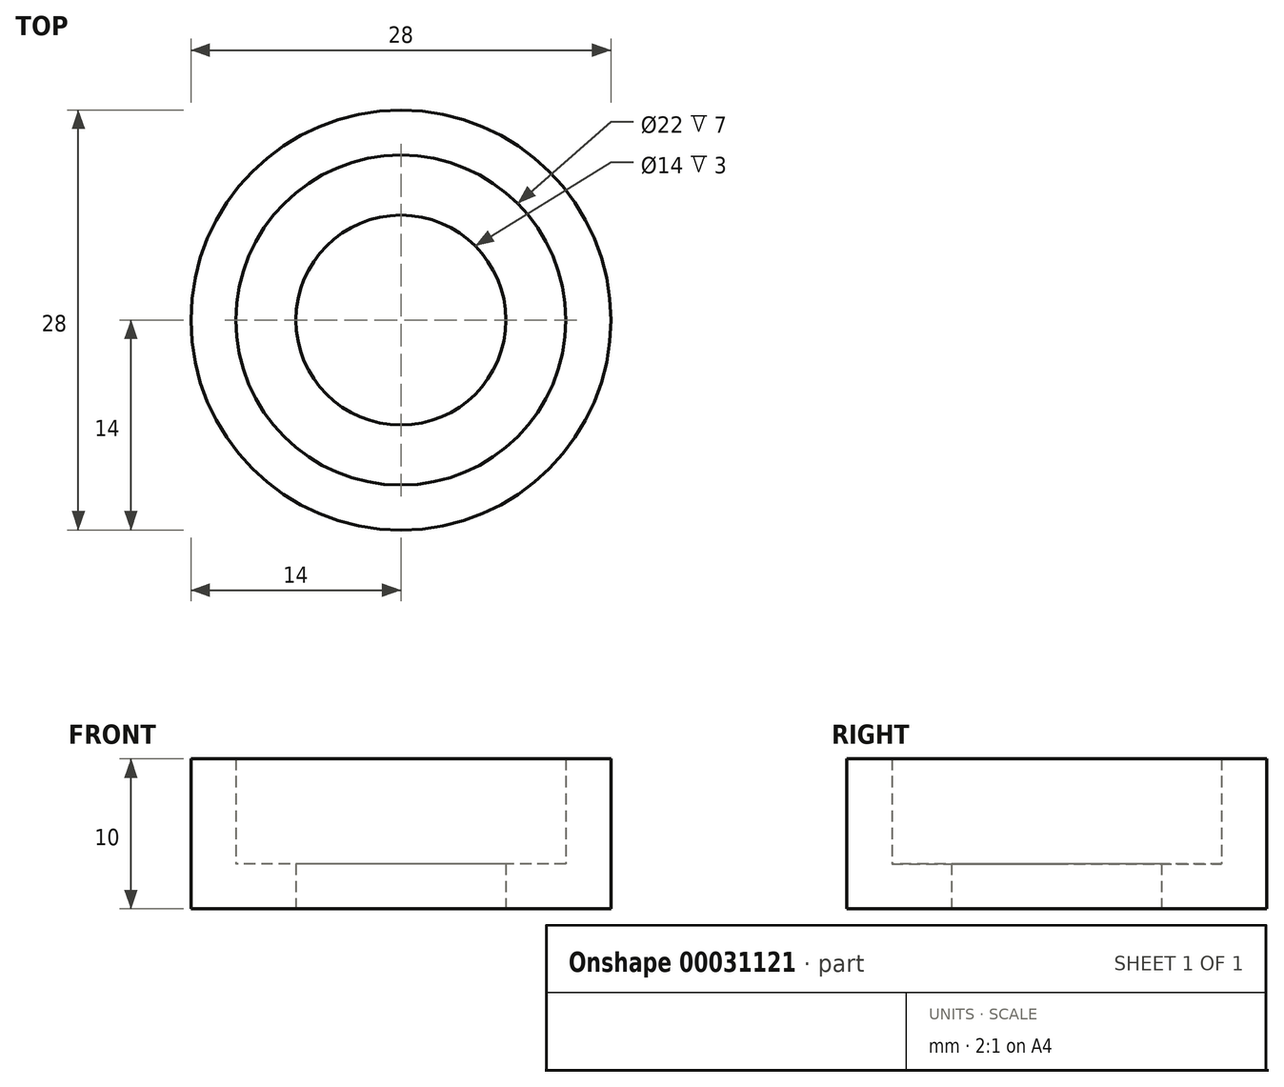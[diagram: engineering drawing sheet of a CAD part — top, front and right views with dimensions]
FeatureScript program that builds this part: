
annotation { "Feature Type Name" : "Feature", "Feature Type Description" : "" }
export const myFeature = defineFeature(function(context is Context, id is Id, definition is map)
    precondition{}
    {
        {
            var Q0;
            Q0=qCreatedBy(makeId("Top.planeOp"),FACE);
            var sketch = newSketch(context, id + "F0", { "sketchPlane" : qUnion([Q0])});
            skCircle(sketch, "E0", {"center": v(0, 0) * mm, "radius": 11 * mm});
            skCircle(sketch, "E1.0", {"center": v(0, 0) * mm, "radius": 14 * mm});
            skCircle(sketch, "E2", {"center": v(0, 0) * mm, "radius": 7 * mm});
            skSolve(sketch);
        }
        {
            var Q0;
            Q0=makeQuery(id+"F0.imprint","IMPRINT",FACE,{"disambiguationData":[TD([[makeQuery(id+"F0.imprint","IMPRINT",EDGE,{"derivedFrom":sQuery(id+"F0.wireOp",EDGE,"E0")}),-1.0]])]});
            extrude(context, id + "F1", {"entities" : qUnion([Q0]), "depth" : 10 * mm});
        }
        {
            var Q0;
            Q0=makeQuery(id+"F0.imprint","IMPRINT",FACE,{"disambiguationData":[TD([[makeQuery(id+"F0.imprint","IMPRINT",EDGE,{"derivedFrom":sQuery(id+"F0.wireOp",EDGE,"E0")}),1.0]])]});
            extrude(context, id + "F2", {"entities" : qUnion([Q0]), "operationType" : NewBodyOperationType.ADD, "depth" : 3 * mm});
        }
        {
            var Q0;
            Q0=qCreatedBy(makeId("Front.planeOp"),FACE);
            cPlane(context, id + "F3", {"entities" : qUnion([Q0]), "cplaneType" : CPlaneType.OFFSET, "offset" : 20 * mm, "width" : 150 * mm, "height" : 150 * mm});
        }
    });
